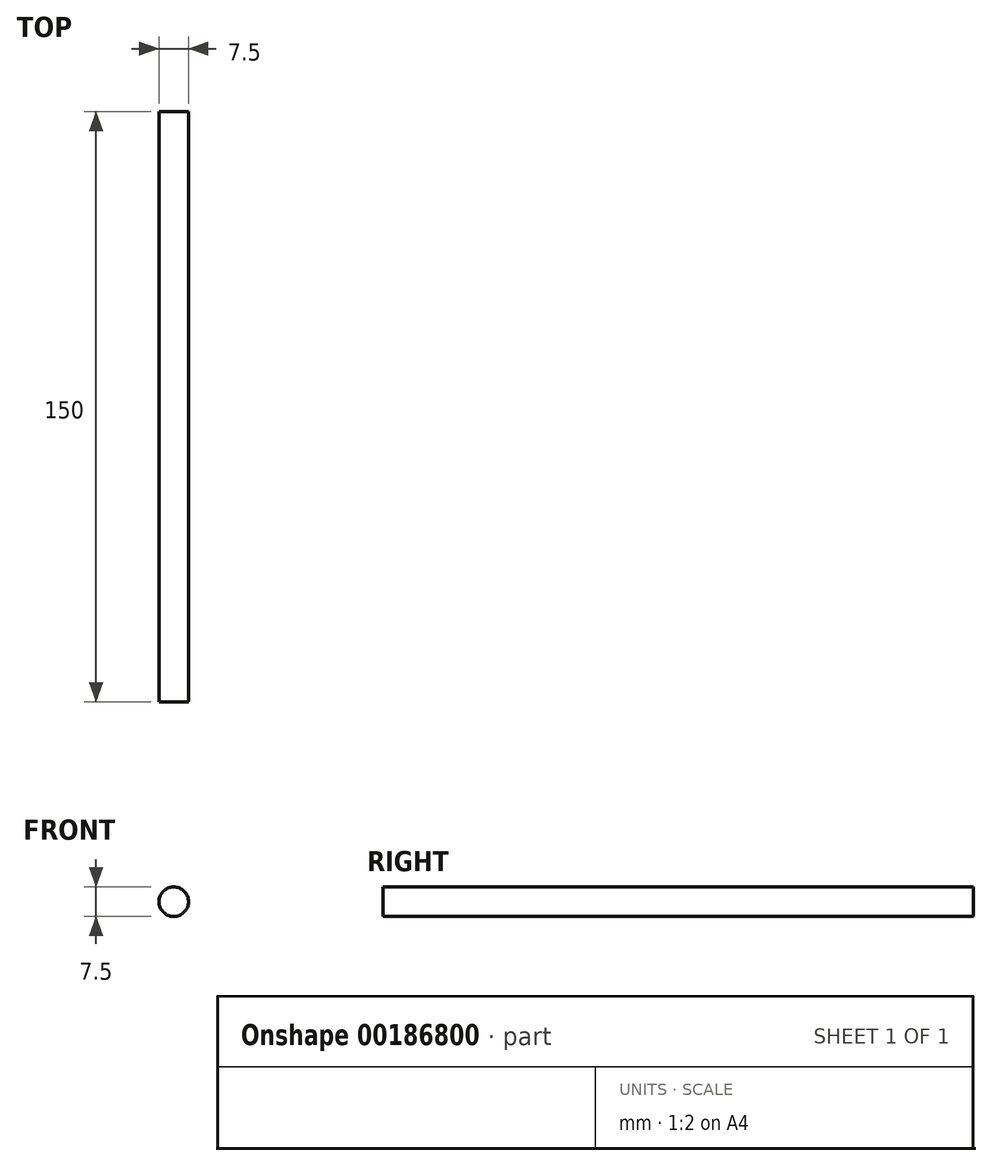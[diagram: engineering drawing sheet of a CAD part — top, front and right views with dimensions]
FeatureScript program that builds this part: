
annotation { "Feature Type Name" : "Feature", "Feature Type Description" : "" }
export const myFeature = defineFeature(function(context is Context, id is Id, definition is map)
    precondition{}
    {
        {
            var Q0;
            Q0=qCreatedBy(makeId("Front.planeOp"),FACE);
            var sketch = newSketch(context, id + "F0", { "sketchPlane" : qUnion([Q0])});
            skCircle(sketch, "E0", {"center": v(-7.7, 9.18) * mm, "radius": 3.75 * mm});
            skSolve(sketch);
        }
        {
            var Q0;
            Q0=makeQuery(id+"F0.imprint","IMPRINT",FACE,{"disambiguationData":[TD([[makeQuery(id+"F0.imprint","IMPRINT",EDGE,{"derivedFrom":sQuery(id+"F0.wireOp",EDGE,"E0")}),1.0]])]});
            extrude(context, id + "F1", {"entities" : qUnion([Q0]), "depth" : 150 * mm});
        }
    });
